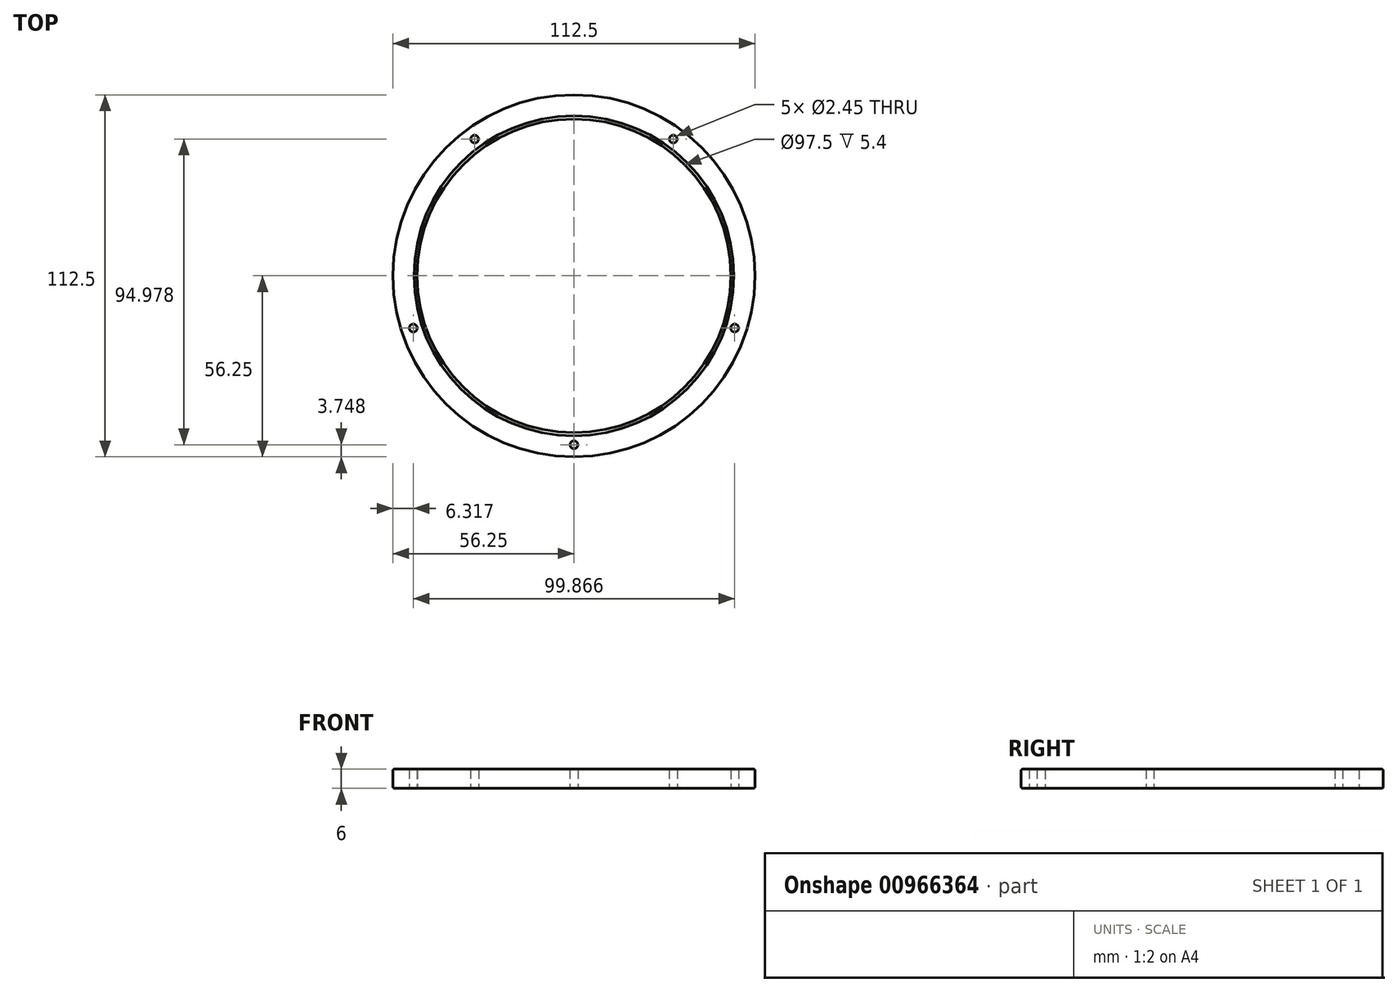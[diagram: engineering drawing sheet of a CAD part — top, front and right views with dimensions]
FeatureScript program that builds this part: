
annotation { "Feature Type Name" : "Feature", "Feature Type Description" : "" }
export const myFeature = defineFeature(function(context is Context, id is Id, definition is map)
    precondition{}
    {
        {
            var Q0;
            Q0=qCreatedBy(makeId("Top.planeOp"),FACE);
            var sketch = newSketch(context, id + "F0", { "sketchPlane" : qUnion([Q0])});
            skCircle(sketch, "E0", {"center": v(0, 0) * mm, "radius": 48.75 * mm});
            skCircle(sketch, "E1", {"center": v(0, 0) * mm, "radius": 56.25 * mm});
            skPoint(sketch, "E2", {"position": v(0, -52.5) * mm});
            skPoint(sketch, "E3.1.0", {"position": v(49.93, -16.22) * mm});
            skPoint(sketch, "E3.2.0", {"position": v(30.86, 42.48) * mm});
            skPoint(sketch, "E3.3.0", {"position": v(-30.86, 42.48) * mm});
            skPoint(sketch, "E3.4.0", {"position": v(-49.93, -16.22) * mm});
            skCircle(sketch, "E4", {"center": v(0, -52.5) * mm, "radius": 1.23 * mm});
            skCircle(sketch, "E5", {"center": v(49.93, -16.22) * mm, "radius": 1.23 * mm});
            skCircle(sketch, "E6", {"center": v(30.86, 42.48) * mm, "radius": 1.23 * mm});
            skCircle(sketch, "E7", {"center": v(-30.86, 42.48) * mm, "radius": 1.23 * mm});
            skCircle(sketch, "E8", {"center": v(-49.93, -16.22) * mm, "radius": 1.23 * mm});
            skSolve(sketch);
        }
        {
            var Q0;
            Q0 = qSketchRegion(id + "F0", true);
            extrude(context, id + "F1", {"entities" : qUnion([Q0]), "depth" : 6 * mm, "offsetDistance" : 25 * mm});
        }
        {
            var Q0;
            Q0=makeQuery(id+"F1.opExtrude","CAP_EDGE",EDGE,{"disambiguationData":[OSD([sQuery(id+"F0.wireOp",EDGE,"E0")])],"isStart":false});
            fillet(context, id + "F2", {"entities" : qUnion([Q0]), "radius" : 1.5 * mm, "tangentPropagation" : true, "allowEdgeOverflow" : false});
        }
        {
            var Q0;
            Q0 = qSketchRegion(id + "F0", true);
            extrude(context, id + "F3", {"entities" : qUnion([Q0]), "operationType" : NewBodyOperationType.ADD, "depth" : 5.9 * mm, "offsetDistance" : 25 * mm});
        }
        {
            var Q0;
            Q0=makeQuery(id+"F1.opExtrude","CAP_EDGE",EDGE,{"disambiguationData":[OSD([sQuery(id+"F0.wireOp",EDGE,"E0")])],"isStart":true});
            var Q1;
            Q1=makeQuery(id+"F1.opExtrude","CAP_EDGE",EDGE,{"disambiguationData":[OSD([sQuery(id+"F0.wireOp",EDGE,"E1")])],"isStart":true});
            var Q2;
            Q2=makeQuery(id+"F1.opExtrude","CAP_EDGE",EDGE,{"disambiguationData":[OSD([sQuery(id+"F0.wireOp",EDGE,"E1")])],"isStart":false});
            fillet(context, id + "F4", {"entities" : qUnion([Q0, Q1, Q2]), "radius" : .5 * mm, "tangentPropagation" : true, "allowEdgeOverflow" : false});
        }
    });
